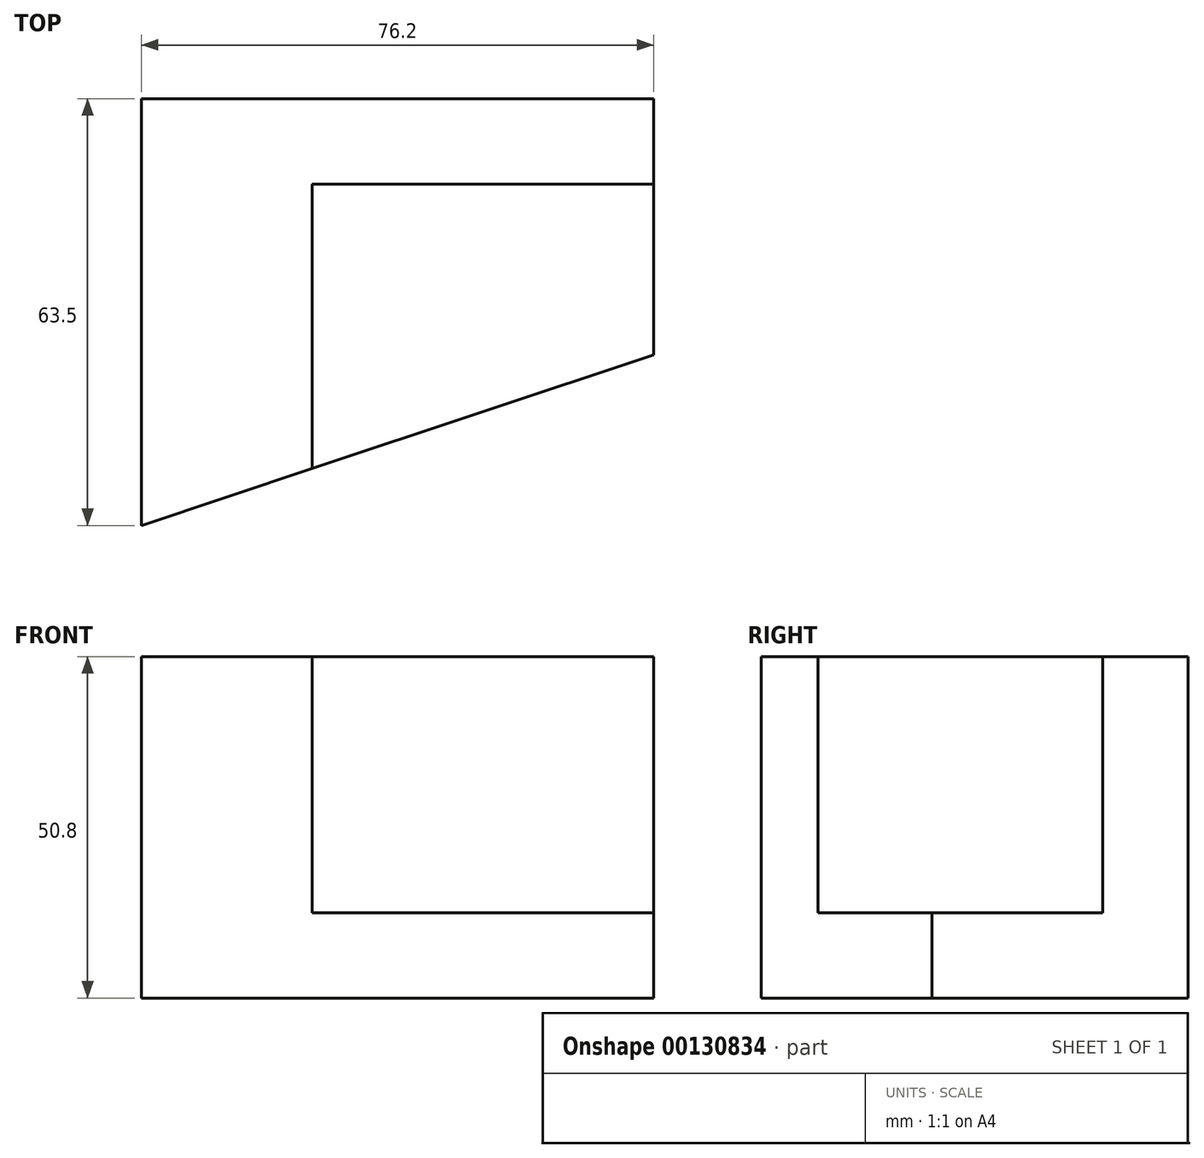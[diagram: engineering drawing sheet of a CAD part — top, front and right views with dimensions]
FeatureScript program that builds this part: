
annotation { "Feature Type Name" : "Feature", "Feature Type Description" : "" }
export const myFeature = defineFeature(function(context is Context, id is Id, definition is map)
    precondition{}
    {
        {
            var Q0;
            Q0=qCreatedBy(makeId("Top.planeOp"),FACE);
            var sketch = newSketch(context, id + "F0", { "sketchPlane" : qUnion([Q0])});
            skLineSegment(sketch, "E0", {"start": v(0, 0) * mm, "end": v(0, 63.5) * mm});
            skLineSegment(sketch, "E1", {"start": v(0, 63.5) * mm, "end": v(76.2, 63.5) * mm});
            skLineSegment(sketch, "E2", {"start": v(76.2, 63.5) * mm, "end": v(76.2, 25.4) * mm});
            skLineSegment(sketch, "E3", {"start": v(76.2, 25.4) * mm, "end": v(0, 0) * mm});
            skSolve(sketch);
        }
        {
            var Q0;
            Q0 = qSketchRegion(id + "F0", true);
            extrude(context, id + "F1", {"entities" : qUnion([Q0]), "depth" : 50.8 * mm});
        }
        {
            var Q0;
            Q0=qCreatedBy(makeId("Top.planeOp"),FACE);
            var sketch = newSketch(context, id + "F2", { "sketchPlane" : qUnion([Q0])});
            skLineSegment(sketch, "E4", {"start": v(25.4, 8.47) * mm, "end": v(25.4, 50.8) * mm});
            skLineSegment(sketch, "E5", {"start": v(25.4, 50.8) * mm, "end": v(76.2, 50.8) * mm});
            skLineSegment(sketch, "E6.0", {"start": v(76.2, 63.5) * mm, "end": v(76.2, 25.4) * mm});
            skLineSegment(sketch, "E7.0", {"start": v(76.2, 25.4) * mm, "end": v(0, 0) * mm});
            skSolve(sketch);
        }
        {
            var Q0;
            Q0 = qSketchRegion(id + "F2", true);
            extrude(context, id + "F3", {"entities" : qUnion([Q0]), "operationType" : NewBodyOperationType.REMOVE, "depth" : 63.08 * mm});
        }
        {
            var Q0;
            Q0 = qSketchRegion(id + "F2", true);
            extrude(context, id + "F4", {"entities" : qUnion([Q0]), "operationType" : NewBodyOperationType.ADD, "depth" : 12.7 * mm});
        }
    });
